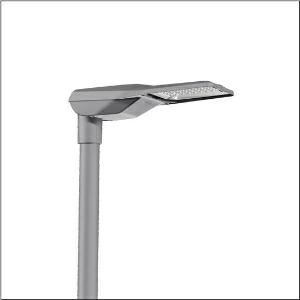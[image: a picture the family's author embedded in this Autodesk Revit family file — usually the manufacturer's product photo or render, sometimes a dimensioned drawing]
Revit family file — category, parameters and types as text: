
# Revit family: streetlight_sl_21_iq_mini___st1_0a_5xe2d41g08hb_63a2
name_source: partatom
category: Lighting Fixtures
units: mm (PartAtom-declared; Revit-internal decimal feet)

## family parameters
Cut with Voids When Loaded = No
Host = Face
Light Source = No
Part Type = Normal
Room Calculation Point = No
Round Connector Dimension = Use Diameter
Shared = No

## types (1)
- --- (1 x LED, 9860 lm, 70.9 W, 4000K)
    Apparent Load = 71 VA
    CIE Flux Codes = 37 72 97 100 100
    Color Rendering = 70
    Color Temperature = 4000K
    Default Elevation = 1800 mm
    Description = Streetlight SL 21 iQ mini, mast luminaire, primary light control with lens, of PMMA, primary optical cover: cover, of toughened safety glass, transparent, light distribution: ST1.0a, light emission: direct distribution, primary light characteristic: asymmetric, installation type: post-top, side-entry, LED, High Power LED, rated luminous flux: 9.860lm, luminous efficacy: 139lm/W, light colour: 740, colour temperature: 4000K, control: Street-Remote, Auto-Match, Temp-Guard, Lumen-Switch, Night-Set, Smart-Wire, Light-Fading, Desk-Remote (wireless, voltage-free reading and setting of iQ features in the workshop via application-optimized NFC function/RFID function), optimised constant luminous flux control (CLO 2.0), presetting dimming linear, mains connection: 220..240V, AC, 50/60Hz, start of lifetime: 71W, end of service life: 75W, reduction: 31W, luminaire housing, of diecast aluminium, powder-coated, Siteco® metallic grey (DB 702S), corrosivity category C5 mid according to DIN EN ISO 12944, please order mast flange separately, inclination adjustable: 0°, 5°, 10°, 15°, sealing non-destructively replaceable, multi-level sealing system, length: 628mm, width: 235mm, height: 110mm, mast flange for spigot size: 42mm (side-entry): 5XC10008XM4, 60/48mm (side-entry/post-top): 5XC10108XM2, 76/60mm (side-entry/post-top): 5XC10108XM1, protection rating (complete): IP66, insulation class (complete): insulation class II (safety insulation), certification: CE, ENEC, ENEC+, VDE, impact resistance: IK09, permissible operating ambient temperature for outdoor applications: -40..+50°C, standard-compliant lighting for roads and squares, packaging unit: 1 piece

Light Distribution: ST1.0a
    Height = 110 mm
    Lamp = 1 x LED
    Lamp Light Flux = 9860 lm
    Lamp Power = 70.9 W
    Lamp count = 1
    Length = 625 mm
    Luminous efficacy = 139 lm/W
    Manufacturer = Siteco
    ModVariant = No
    Model = 5XE2D41G08HB
    Number of Poles = 1
    OnlyDefault = Yes
    Power Factor = 1
    Product Name = Streetlight SL 21 iQ mini | ST1.0a
    Product group = mast luminaire | pylon top
    ProductGroupID = 6100
    Protection Class = Protection class II
    Protection Degree = IP 66
    RLX_Detail_Level = 1
    RLX_Emergency_Light_Flux = 0 lm
    RLX_Emergency_Type = 0
    RLX_Emergency_Type_DB = No
    RlxData = <blob elided: 93833 chars, md5=bee28e8b>
    Socket = socket
    Standby Power = 0 W
    System Light Flux = 9860 lm
    System Power = 71 W
    Type Comments = factory setting: luminous flux: 100 % | dim-lin: 254 | 711 mA
    Type Image = l_1003519.jpg
    URL = http://relux.com
    VarID = @adj_090381
    Voltage = 0 V
    Weight = 0.00 kg
    Width = 234 mm

## geometry (parser evidence)
native form markers: Blend x4, Sweep x10
no freeform markers — native parametric forms only
